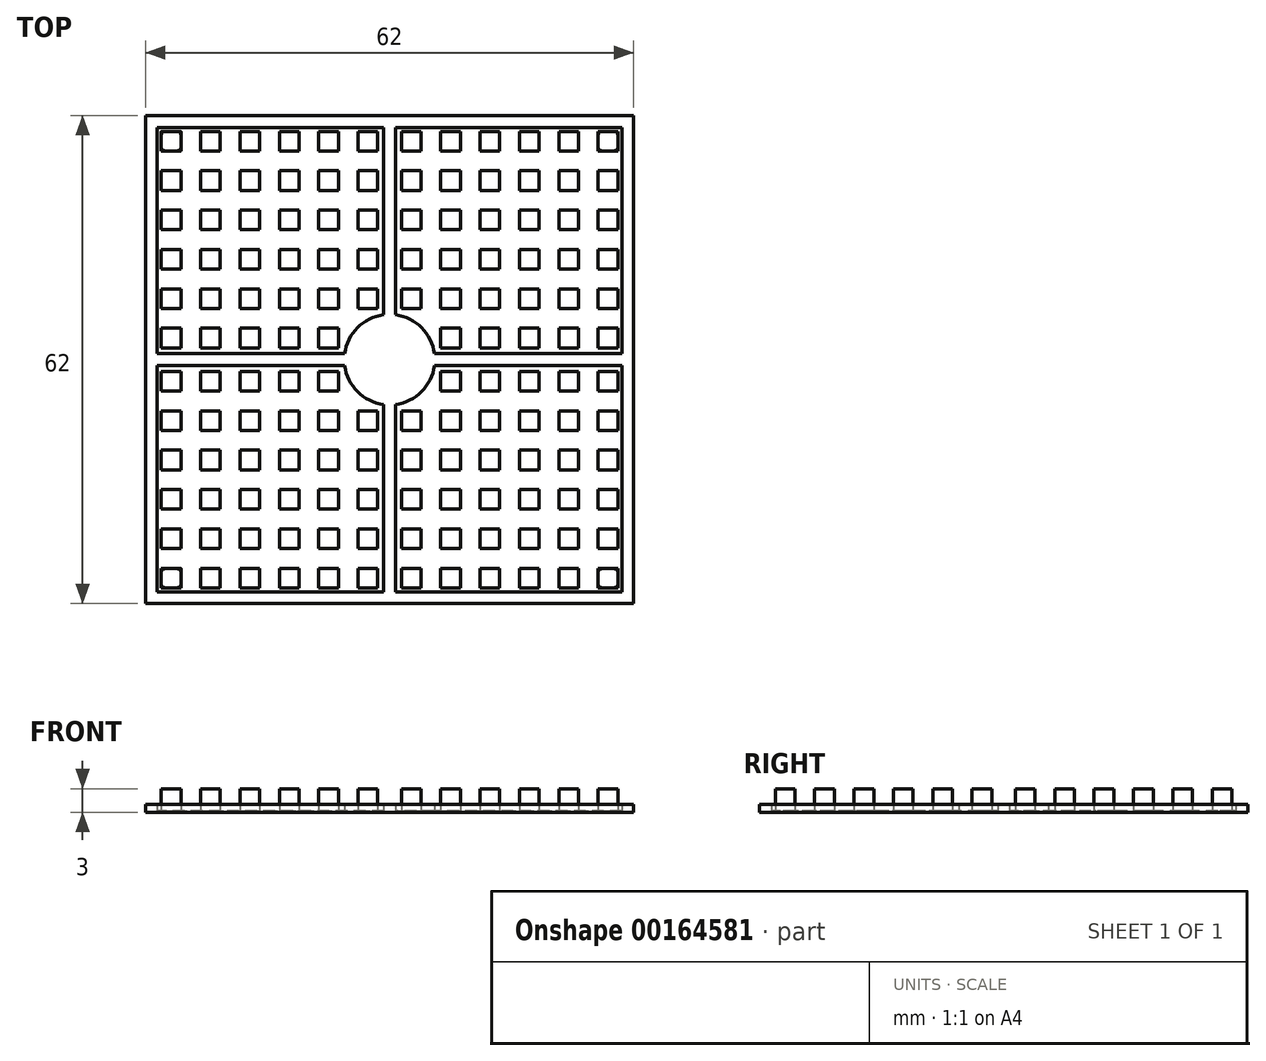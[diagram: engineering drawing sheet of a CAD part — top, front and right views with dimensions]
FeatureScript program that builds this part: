
annotation { "Feature Type Name" : "Feature", "Feature Type Description" : "" }
export const myFeature = defineFeature(function(context is Context, id is Id, definition is map)
    precondition{}
    {
        {
            var Q0;
            Q0=qCreatedBy(makeId("Top.planeOp"),FACE);
            var sketch = newSketch(context, id + "F0", { "sketchPlane" : qUnion([Q0])});
            skArc(sketch, "E0", {"start": v(-5.7, -0.75) * mm, "mid": v(-4.07, -4.07) * mm, "end": v(-0.75, -5.7) * mm});
            skLineSegment(sketch, "E1.bottom", {"start": v(31, 31) * mm, "end": v(-31, 31) * mm});
            skLineSegment(sketch, "E1.top", {"start": v(31, -31) * mm, "end": v(-31, -31) * mm});
            skLineSegment(sketch, "E1.left", {"start": v(31, 31) * mm, "end": v(31, -31) * mm});
            skLineSegment(sketch, "E1.right", {"start": v(-31, 31) * mm, "end": v(-31, -31) * mm});
            skLineSegment(sketch, "E2.bottom", {"start": v(-0.75, 29.5) * mm, "end": v(-29.5, 29.5) * mm});
            skLineSegment(sketch, "E2.top", {"start": v(-0.75, -29.5) * mm, "end": v(-29.5, -29.5) * mm});
            skLineSegment(sketch, "E2.right", {"start": v(-29.5, 29.5) * mm, "end": v(-29.5, -29.5) * mm});
            skLineSegment(sketch, "E3", {"start": v(0, 5.75) * mm, "end": v(0, 31) * mm, "construction": true});
            skLineSegment(sketch, "E4", {"start": v(0, 0) * mm, "end": v(31, 0) * mm, "construction": true});
            skLineSegment(sketch, "E5", {"start": v(0, -5.75) * mm, "end": v(0, -29.5) * mm, "construction": true});
            skLineSegment(sketch, "E6", {"start": v(0, 0) * mm, "end": v(-0.75, 0) * mm, "construction": true});
            skLineSegment(sketch, "E7", {"start": v(-0.75, 29.5) * mm, "end": v(-0.75, 5.7) * mm});
            skLineSegment(sketch, "E8", {"start": v(-29.5, -0.75) * mm, "end": v(-5.7, -0.75) * mm});
            skLineSegment(sketch, "E9", {"start": v(-29.5, 0.75) * mm, "end": v(-5.7, 0.75) * mm});
            skLineSegment(sketch, "E10.trimOffspring", {"start": v(-5.75, 0) * mm, "end": v(-31, 0) * mm, "construction": true});
            skArc(sketch, "E11.trimOffspring", {"start": v(-0.75, 5.7) * mm, "mid": v(-4.07, 4.07) * mm, "end": v(-5.7, 0.75) * mm});
            skPoint(sketch, "E12.orphan", {"position": v(29.5, -29.5) * mm});
            skPoint(sketch, "E13.orphan", {"position": v(29.5, 29.5) * mm});
            skLineSegment(sketch, "E14.MirrorCS", {"start": v(0.75, 29.5) * mm, "end": v(0.75, 5.7) * mm});
            skLineSegment(sketch, "E15.MirrorCS", {"start": v(0.75, 29.5) * mm, "end": v(29.5, 29.5) * mm});
            skLineSegment(sketch, "E16.MirrorCS", {"start": v(29.5, 29.5) * mm, "end": v(29.5, -29.5) * mm});
            skLineSegment(sketch, "E17.MirrorCS", {"start": v(29.5, 0.75) * mm, "end": v(5.7, 0.75) * mm});
            skLineSegment(sketch, "E18.MirrorCS", {"start": v(29.5, -0.75) * mm, "end": v(5.7, -0.75) * mm});
            skArc(sketch, "E19.MirrorCS", {"start": v(5.7, -0.75) * mm, "mid": v(4.07, -4.07) * mm, "end": v(0.75, -5.7) * mm});
            skArc(sketch, "E20.MirrorCS", {"start": v(0.75, 5.7) * mm, "mid": v(4.07, 4.07) * mm, "end": v(5.7, 0.75) * mm});
            skLineSegment(sketch, "E21.trimOffspring", {"start": v(-0.75, -5.7) * mm, "end": v(-0.75, -29.5) * mm});
            skLineSegment(sketch, "E22.trimOffspring", {"start": v(0.75, -5.7) * mm, "end": v(0.75, -29.5) * mm});
            skPoint(sketch, "E23.orphan", {"position": v(0, -5.75) * mm});
            skPoint(sketch, "E24.orphan", {"position": v(0, 5.75) * mm});
            skLineSegment(sketch, "E25.MirrorCS", {"start": v(0.75, -29.5) * mm, "end": v(29.5, -29.5) * mm});
            skPoint(sketch, "E26.orphan", {"position": v(0, -31) * mm});
            skPoint(sketch, "E27.orphan", {"position": v(0, -29.5) * mm});
            skPoint(sketch, "E28.orphan", {"position": v(0, 29.5) * mm});
            skSolve(sketch);
        }
        {
            var Q0;
            Q0 = qSketchRegion(id + "F0", true);
            extrude(context, id + "F1", {"entities" : qUnion([Q0]), "depth" : 1 * mm});
        }
        {
            var Q0;
            Q0=qCreatedBy(makeId("Top.planeOp"),FACE);
            var sketch = newSketch(context, id + "F2", { "sketchPlane" : qUnion([Q0])});
            skLineSegment(sketch, "E29.bottom", {"start": v(-29, 29) * mm, "end": v(-26.5, 29) * mm});
            skLineSegment(sketch, "E29.top", {"start": v(-29, 26.5) * mm, "end": v(-26.5, 26.5) * mm});
            skLineSegment(sketch, "E29.left", {"start": v(-29, 29) * mm, "end": v(-29, 26.5) * mm});
            skLineSegment(sketch, "E29.right", {"start": v(-26.5, 29) * mm, "end": v(-26.5, 26.5) * mm});
            skLineSegment(sketch, "E30.0.1.0", {"start": v(-29, 24) * mm, "end": v(-26.5, 24) * mm});
            skLineSegment(sketch, "E30.0.1.1", {"start": v(-29, 21.5) * mm, "end": v(-26.5, 21.5) * mm});
            skLineSegment(sketch, "E30.0.1.2", {"start": v(-29, 24) * mm, "end": v(-29, 21.5) * mm});
            skLineSegment(sketch, "E30.0.1.3", {"start": v(-26.5, 24) * mm, "end": v(-26.5, 21.5) * mm});
            skLineSegment(sketch, "E30.0.2.0", {"start": v(-29, 19) * mm, "end": v(-26.5, 19) * mm});
            skLineSegment(sketch, "E30.0.2.1", {"start": v(-29, 16.5) * mm, "end": v(-26.5, 16.5) * mm});
            skLineSegment(sketch, "E30.0.2.2", {"start": v(-29, 19) * mm, "end": v(-29, 16.5) * mm});
            skLineSegment(sketch, "E30.0.2.3", {"start": v(-26.5, 19) * mm, "end": v(-26.5, 16.5) * mm});
            skLineSegment(sketch, "E30.0.3.0", {"start": v(-29, 14) * mm, "end": v(-26.5, 14) * mm});
            skLineSegment(sketch, "E30.0.3.1", {"start": v(-29, 11.5) * mm, "end": v(-26.5, 11.5) * mm});
            skLineSegment(sketch, "E30.0.3.2", {"start": v(-29, 14) * mm, "end": v(-29, 11.5) * mm});
            skLineSegment(sketch, "E30.0.3.3", {"start": v(-26.5, 14) * mm, "end": v(-26.5, 11.5) * mm});
            skLineSegment(sketch, "E30.0.4.0", {"start": v(-29, 9) * mm, "end": v(-26.5, 9) * mm});
            skLineSegment(sketch, "E30.0.4.1", {"start": v(-29, 6.5) * mm, "end": v(-26.5, 6.5) * mm});
            skLineSegment(sketch, "E30.0.4.2", {"start": v(-29, 9) * mm, "end": v(-29, 6.5) * mm});
            skLineSegment(sketch, "E30.0.4.3", {"start": v(-26.5, 9) * mm, "end": v(-26.5, 6.5) * mm});
            skLineSegment(sketch, "E30.0.5.0", {"start": v(-29, 4) * mm, "end": v(-26.5, 4) * mm});
            skLineSegment(sketch, "E30.0.5.1", {"start": v(-29, 1.5) * mm, "end": v(-26.5, 1.5) * mm});
            skLineSegment(sketch, "E30.0.5.2", {"start": v(-29, 4) * mm, "end": v(-29, 1.5) * mm});
            skLineSegment(sketch, "E30.0.5.3", {"start": v(-26.5, 4) * mm, "end": v(-26.5, 1.5) * mm});
            skLineSegment(sketch, "E30.1.0.0", {"start": v(-24, 29) * mm, "end": v(-21.5, 29) * mm});
            skLineSegment(sketch, "E30.1.0.1", {"start": v(-24, 26.5) * mm, "end": v(-21.5, 26.5) * mm});
            skLineSegment(sketch, "E30.1.0.2", {"start": v(-24, 29) * mm, "end": v(-24, 26.5) * mm});
            skLineSegment(sketch, "E30.1.0.3", {"start": v(-21.5, 29) * mm, "end": v(-21.5, 26.5) * mm});
            skLineSegment(sketch, "E30.1.1.0", {"start": v(-24, 24) * mm, "end": v(-21.5, 24) * mm});
            skLineSegment(sketch, "E30.1.1.1", {"start": v(-24, 21.5) * mm, "end": v(-21.5, 21.5) * mm});
            skLineSegment(sketch, "E30.1.1.2", {"start": v(-24, 24) * mm, "end": v(-24, 21.5) * mm});
            skLineSegment(sketch, "E30.1.1.3", {"start": v(-21.5, 24) * mm, "end": v(-21.5, 21.5) * mm});
            skLineSegment(sketch, "E30.1.2.0", {"start": v(-24, 19) * mm, "end": v(-21.5, 19) * mm});
            skLineSegment(sketch, "E30.1.2.1", {"start": v(-24, 16.5) * mm, "end": v(-21.5, 16.5) * mm});
            skLineSegment(sketch, "E30.1.2.2", {"start": v(-24, 19) * mm, "end": v(-24, 16.5) * mm});
            skLineSegment(sketch, "E30.1.2.3", {"start": v(-21.5, 19) * mm, "end": v(-21.5, 16.5) * mm});
            skLineSegment(sketch, "E30.1.3.0", {"start": v(-24, 14) * mm, "end": v(-21.5, 14) * mm});
            skLineSegment(sketch, "E30.1.3.1", {"start": v(-24, 11.5) * mm, "end": v(-21.5, 11.5) * mm});
            skLineSegment(sketch, "E30.1.3.2", {"start": v(-24, 14) * mm, "end": v(-24, 11.5) * mm});
            skLineSegment(sketch, "E30.1.3.3", {"start": v(-21.5, 14) * mm, "end": v(-21.5, 11.5) * mm});
            skLineSegment(sketch, "E30.1.4.0", {"start": v(-24, 9) * mm, "end": v(-21.5, 9) * mm});
            skLineSegment(sketch, "E30.1.4.1", {"start": v(-24, 6.5) * mm, "end": v(-21.5, 6.5) * mm});
            skLineSegment(sketch, "E30.1.4.2", {"start": v(-24, 9) * mm, "end": v(-24, 6.5) * mm});
            skLineSegment(sketch, "E30.1.4.3", {"start": v(-21.5, 9) * mm, "end": v(-21.5, 6.5) * mm});
            skLineSegment(sketch, "E30.1.5.0", {"start": v(-24, 4) * mm, "end": v(-21.5, 4) * mm});
            skLineSegment(sketch, "E30.1.5.1", {"start": v(-24, 1.5) * mm, "end": v(-21.5, 1.5) * mm});
            skLineSegment(sketch, "E30.1.5.2", {"start": v(-24, 4) * mm, "end": v(-24, 1.5) * mm});
            skLineSegment(sketch, "E30.1.5.3", {"start": v(-21.5, 4) * mm, "end": v(-21.5, 1.5) * mm});
            skLineSegment(sketch, "E30.2.0.0", {"start": v(-19, 29) * mm, "end": v(-16.5, 29) * mm});
            skLineSegment(sketch, "E30.2.0.1", {"start": v(-19, 26.5) * mm, "end": v(-16.5, 26.5) * mm});
            skLineSegment(sketch, "E30.2.0.2", {"start": v(-19, 29) * mm, "end": v(-19, 26.5) * mm});
            skLineSegment(sketch, "E30.2.0.3", {"start": v(-16.5, 29) * mm, "end": v(-16.5, 26.5) * mm});
            skLineSegment(sketch, "E30.2.1.0", {"start": v(-19, 24) * mm, "end": v(-16.5, 24) * mm});
            skLineSegment(sketch, "E30.2.1.1", {"start": v(-19, 21.5) * mm, "end": v(-16.5, 21.5) * mm});
            skLineSegment(sketch, "E30.2.1.2", {"start": v(-19, 24) * mm, "end": v(-19, 21.5) * mm});
            skLineSegment(sketch, "E30.2.1.3", {"start": v(-16.5, 24) * mm, "end": v(-16.5, 21.5) * mm});
            skLineSegment(sketch, "E30.2.2.0", {"start": v(-19, 19) * mm, "end": v(-16.5, 19) * mm});
            skLineSegment(sketch, "E30.2.2.1", {"start": v(-19, 16.5) * mm, "end": v(-16.5, 16.5) * mm});
            skLineSegment(sketch, "E30.2.2.2", {"start": v(-19, 19) * mm, "end": v(-19, 16.5) * mm});
            skLineSegment(sketch, "E30.2.2.3", {"start": v(-16.5, 19) * mm, "end": v(-16.5, 16.5) * mm});
            skLineSegment(sketch, "E30.2.3.0", {"start": v(-19, 14) * mm, "end": v(-16.5, 14) * mm});
            skLineSegment(sketch, "E30.2.3.1", {"start": v(-19, 11.5) * mm, "end": v(-16.5, 11.5) * mm});
            skLineSegment(sketch, "E30.2.3.2", {"start": v(-19, 14) * mm, "end": v(-19, 11.5) * mm});
            skLineSegment(sketch, "E30.2.3.3", {"start": v(-16.5, 14) * mm, "end": v(-16.5, 11.5) * mm});
            skLineSegment(sketch, "E30.2.4.0", {"start": v(-19, 9) * mm, "end": v(-16.5, 9) * mm});
            skLineSegment(sketch, "E30.2.4.1", {"start": v(-19, 6.5) * mm, "end": v(-16.5, 6.5) * mm});
            skLineSegment(sketch, "E30.2.4.2", {"start": v(-19, 9) * mm, "end": v(-19, 6.5) * mm});
            skLineSegment(sketch, "E30.2.4.3", {"start": v(-16.5, 9) * mm, "end": v(-16.5, 6.5) * mm});
            skLineSegment(sketch, "E30.2.5.0", {"start": v(-19, 4) * mm, "end": v(-16.5, 4) * mm});
            skLineSegment(sketch, "E30.2.5.1", {"start": v(-19, 1.5) * mm, "end": v(-16.5, 1.5) * mm});
            skLineSegment(sketch, "E30.2.5.2", {"start": v(-19, 4) * mm, "end": v(-19, 1.5) * mm});
            skLineSegment(sketch, "E30.2.5.3", {"start": v(-16.5, 4) * mm, "end": v(-16.5, 1.5) * mm});
            skLineSegment(sketch, "E30.3.0.0", {"start": v(-14, 29) * mm, "end": v(-11.5, 29) * mm});
            skLineSegment(sketch, "E30.3.0.1", {"start": v(-14, 26.5) * mm, "end": v(-11.5, 26.5) * mm});
            skLineSegment(sketch, "E30.3.0.2", {"start": v(-14, 29) * mm, "end": v(-14, 26.5) * mm});
            skLineSegment(sketch, "E30.3.0.3", {"start": v(-11.5, 29) * mm, "end": v(-11.5, 26.5) * mm});
            skLineSegment(sketch, "E30.3.1.0", {"start": v(-14, 24) * mm, "end": v(-11.5, 24) * mm});
            skLineSegment(sketch, "E30.3.1.1", {"start": v(-14, 21.5) * mm, "end": v(-11.5, 21.5) * mm});
            skLineSegment(sketch, "E30.3.1.2", {"start": v(-14, 24) * mm, "end": v(-14, 21.5) * mm});
            skLineSegment(sketch, "E30.3.1.3", {"start": v(-11.5, 24) * mm, "end": v(-11.5, 21.5) * mm});
            skLineSegment(sketch, "E30.3.2.0", {"start": v(-14, 19) * mm, "end": v(-11.5, 19) * mm});
            skLineSegment(sketch, "E30.3.2.1", {"start": v(-14, 16.5) * mm, "end": v(-11.5, 16.5) * mm});
            skLineSegment(sketch, "E30.3.2.2", {"start": v(-14, 19) * mm, "end": v(-14, 16.5) * mm});
            skLineSegment(sketch, "E30.3.2.3", {"start": v(-11.5, 19) * mm, "end": v(-11.5, 16.5) * mm});
            skLineSegment(sketch, "E30.3.3.0", {"start": v(-14, 14) * mm, "end": v(-11.5, 14) * mm});
            skLineSegment(sketch, "E30.3.3.1", {"start": v(-14, 11.5) * mm, "end": v(-11.5, 11.5) * mm});
            skLineSegment(sketch, "E30.3.3.2", {"start": v(-14, 14) * mm, "end": v(-14, 11.5) * mm});
            skLineSegment(sketch, "E30.3.3.3", {"start": v(-11.5, 14) * mm, "end": v(-11.5, 11.5) * mm});
            skLineSegment(sketch, "E30.3.4.0", {"start": v(-14, 9) * mm, "end": v(-11.5, 9) * mm});
            skLineSegment(sketch, "E30.3.4.1", {"start": v(-14, 6.5) * mm, "end": v(-11.5, 6.5) * mm});
            skLineSegment(sketch, "E30.3.4.2", {"start": v(-14, 9) * mm, "end": v(-14, 6.5) * mm});
            skLineSegment(sketch, "E30.3.4.3", {"start": v(-11.5, 9) * mm, "end": v(-11.5, 6.5) * mm});
            skLineSegment(sketch, "E30.3.5.0", {"start": v(-14, 4) * mm, "end": v(-11.5, 4) * mm});
            skLineSegment(sketch, "E30.3.5.1", {"start": v(-14, 1.5) * mm, "end": v(-11.5, 1.5) * mm});
            skLineSegment(sketch, "E30.3.5.2", {"start": v(-14, 4) * mm, "end": v(-14, 1.5) * mm});
            skLineSegment(sketch, "E30.3.5.3", {"start": v(-11.5, 4) * mm, "end": v(-11.5, 1.5) * mm});
            skLineSegment(sketch, "E30.4.0.0", {"start": v(-9, 29) * mm, "end": v(-6.5, 29) * mm});
            skLineSegment(sketch, "E30.4.0.1", {"start": v(-9, 26.5) * mm, "end": v(-6.5, 26.5) * mm});
            skLineSegment(sketch, "E30.4.0.2", {"start": v(-9, 29) * mm, "end": v(-9, 26.5) * mm});
            skLineSegment(sketch, "E30.4.0.3", {"start": v(-6.5, 29) * mm, "end": v(-6.5, 26.5) * mm});
            skLineSegment(sketch, "E30.4.1.0", {"start": v(-9, 24) * mm, "end": v(-6.5, 24) * mm});
            skLineSegment(sketch, "E30.4.1.1", {"start": v(-9, 21.5) * mm, "end": v(-6.5, 21.5) * mm});
            skLineSegment(sketch, "E30.4.1.2", {"start": v(-9, 24) * mm, "end": v(-9, 21.5) * mm});
            skLineSegment(sketch, "E30.4.1.3", {"start": v(-6.5, 24) * mm, "end": v(-6.5, 21.5) * mm});
            skLineSegment(sketch, "E30.4.2.0", {"start": v(-9, 19) * mm, "end": v(-6.5, 19) * mm});
            skLineSegment(sketch, "E30.4.2.1", {"start": v(-9, 16.5) * mm, "end": v(-6.5, 16.5) * mm});
            skLineSegment(sketch, "E30.4.2.2", {"start": v(-9, 19) * mm, "end": v(-9, 16.5) * mm});
            skLineSegment(sketch, "E30.4.2.3", {"start": v(-6.5, 19) * mm, "end": v(-6.5, 16.5) * mm});
            skLineSegment(sketch, "E30.4.3.0", {"start": v(-9, 14) * mm, "end": v(-6.5, 14) * mm});
            skLineSegment(sketch, "E30.4.3.1", {"start": v(-9, 11.5) * mm, "end": v(-6.5, 11.5) * mm});
            skLineSegment(sketch, "E30.4.3.2", {"start": v(-9, 14) * mm, "end": v(-9, 11.5) * mm});
            skLineSegment(sketch, "E30.4.3.3", {"start": v(-6.5, 14) * mm, "end": v(-6.5, 11.5) * mm});
            skLineSegment(sketch, "E30.4.4.0", {"start": v(-9, 9) * mm, "end": v(-6.5, 9) * mm});
            skLineSegment(sketch, "E30.4.4.1", {"start": v(-9, 6.5) * mm, "end": v(-6.5, 6.5) * mm});
            skLineSegment(sketch, "E30.4.4.2", {"start": v(-9, 9) * mm, "end": v(-9, 6.5) * mm});
            skLineSegment(sketch, "E30.4.4.3", {"start": v(-6.5, 9) * mm, "end": v(-6.5, 6.5) * mm});
            skLineSegment(sketch, "E30.4.5.0", {"start": v(-9, 4) * mm, "end": v(-6.5, 4) * mm});
            skLineSegment(sketch, "E30.4.5.1", {"start": v(-9, 1.5) * mm, "end": v(-6.5, 1.5) * mm});
            skLineSegment(sketch, "E30.4.5.2", {"start": v(-9, 4) * mm, "end": v(-9, 1.5) * mm});
            skLineSegment(sketch, "E30.4.5.3", {"start": v(-6.5, 4) * mm, "end": v(-6.5, 1.5) * mm});
            skLineSegment(sketch, "E30.5.0.0", {"start": v(-4, 29) * mm, "end": v(-1.5, 29) * mm});
            skLineSegment(sketch, "E30.5.0.1", {"start": v(-4, 26.5) * mm, "end": v(-1.5, 26.5) * mm});
            skLineSegment(sketch, "E30.5.0.2", {"start": v(-4, 29) * mm, "end": v(-4, 26.5) * mm});
            skLineSegment(sketch, "E30.5.0.3", {"start": v(-1.5, 29) * mm, "end": v(-1.5, 26.5) * mm});
            skLineSegment(sketch, "E30.5.1.0", {"start": v(-4, 24) * mm, "end": v(-1.5, 24) * mm});
            skLineSegment(sketch, "E30.5.1.1", {"start": v(-4, 21.5) * mm, "end": v(-1.5, 21.5) * mm});
            skLineSegment(sketch, "E30.5.1.2", {"start": v(-4, 24) * mm, "end": v(-4, 21.5) * mm});
            skLineSegment(sketch, "E30.5.1.3", {"start": v(-1.5, 24) * mm, "end": v(-1.5, 21.5) * mm});
            skLineSegment(sketch, "E30.5.2.0", {"start": v(-4, 19) * mm, "end": v(-1.5, 19) * mm});
            skLineSegment(sketch, "E30.5.2.1", {"start": v(-4, 16.5) * mm, "end": v(-1.5, 16.5) * mm});
            skLineSegment(sketch, "E30.5.2.2", {"start": v(-4, 19) * mm, "end": v(-4, 16.5) * mm});
            skLineSegment(sketch, "E30.5.2.3", {"start": v(-1.5, 19) * mm, "end": v(-1.5, 16.5) * mm});
            skLineSegment(sketch, "E30.5.3.0", {"start": v(-4, 14) * mm, "end": v(-1.5, 14) * mm});
            skLineSegment(sketch, "E30.5.3.1", {"start": v(-4, 11.5) * mm, "end": v(-1.5, 11.5) * mm});
            skLineSegment(sketch, "E30.5.3.2", {"start": v(-4, 14) * mm, "end": v(-4, 11.5) * mm});
            skLineSegment(sketch, "E30.5.3.3", {"start": v(-1.5, 14) * mm, "end": v(-1.5, 11.5) * mm});
            skLineSegment(sketch, "E30.5.4.0", {"start": v(-4, 9) * mm, "end": v(-1.5, 9) * mm});
            skLineSegment(sketch, "E30.5.4.1", {"start": v(-4, 6.5) * mm, "end": v(-1.5, 6.5) * mm});
            skLineSegment(sketch, "E30.5.4.2", {"start": v(-4, 9) * mm, "end": v(-4, 6.5) * mm});
            skLineSegment(sketch, "E30.5.4.3", {"start": v(-1.5, 9) * mm, "end": v(-1.5, 6.5) * mm});
            skLineSegment(sketch, "E30.5.5.0", {"start": v(-4, 4) * mm, "end": v(-1.5, 4) * mm});
            skLineSegment(sketch, "E30.5.5.1", {"start": v(-4, 1.5) * mm, "end": v(-1.5, 1.5) * mm});
            skLineSegment(sketch, "E30.5.5.2", {"start": v(-4, 4) * mm, "end": v(-4, 1.5) * mm});
            skLineSegment(sketch, "E30.5.5.3", {"start": v(-1.5, 4) * mm, "end": v(-1.5, 1.5) * mm});
            skLineSegment(sketch, "E30.direction1", {"start": v(-29, 26.5) * mm, "end": v(-24, 26.5) * mm, "construction": true});
            skLineSegment(sketch, "E30.direction2", {"start": v(-29, 26.5) * mm, "end": v(-29, 21.5) * mm, "construction": true});
            skSolve(sketch);
        }
        {
            var Q0;
            Q0=makeQuery(id+"F2.imprint","IMPRINT",FACE,{"disambiguationData":[TD([[makeQuery(id+"F2.imprint","IMPRINT",EDGE,{"derivedFrom":sQuery(id+"F2.wireOp",EDGE,"E29.bottom")}),-1.0]])]});
            var Q1;
            Q1=makeQuery(id+"F2.imprint","IMPRINT",FACE,{"disambiguationData":[TD([[makeQuery(id+"F2.imprint","IMPRINT",EDGE,{"derivedFrom":sQuery(id+"F2.wireOp",EDGE,"E30.1.0.0")}),-1.0]])]});
            var Q2;
            Q2=makeQuery(id+"F2.imprint","IMPRINT",FACE,{"disambiguationData":[TD([[makeQuery(id+"F2.imprint","IMPRINT",EDGE,{"derivedFrom":sQuery(id+"F2.wireOp",EDGE,"E30.2.0.0")}),-1.0]])]});
            var Q3;
            Q3=makeQuery(id+"F2.imprint","IMPRINT",FACE,{"disambiguationData":[TD([[makeQuery(id+"F2.imprint","IMPRINT",EDGE,{"derivedFrom":sQuery(id+"F2.wireOp",EDGE,"E30.3.0.0")}),-1.0]])]});
            var Q4;
            Q4=makeQuery(id+"F2.imprint","IMPRINT",FACE,{"disambiguationData":[TD([[makeQuery(id+"F2.imprint","IMPRINT",EDGE,{"derivedFrom":sQuery(id+"F2.wireOp",EDGE,"E30.4.0.0")}),-1.0]])]});
            var Q5;
            Q5=makeQuery(id+"F2.imprint","IMPRINT",FACE,{"disambiguationData":[TD([[makeQuery(id+"F2.imprint","IMPRINT",EDGE,{"derivedFrom":sQuery(id+"F2.wireOp",EDGE,"E30.5.0.0")}),-1.0]])]});
            var Q6;
            Q6=makeQuery(id+"F2.imprint","IMPRINT",FACE,{"disambiguationData":[TD([[makeQuery(id+"F2.imprint","IMPRINT",EDGE,{"derivedFrom":sQuery(id+"F2.wireOp",EDGE,"E30.5.1.0")}),-1.0]])]});
            var Q7;
            Q7=makeQuery(id+"F2.imprint","IMPRINT",FACE,{"disambiguationData":[TD([[makeQuery(id+"F2.imprint","IMPRINT",EDGE,{"derivedFrom":sQuery(id+"F2.wireOp",EDGE,"E30.4.1.0")}),-1.0]])]});
            var Q8;
            Q8=makeQuery(id+"F2.imprint","IMPRINT",FACE,{"disambiguationData":[TD([[makeQuery(id+"F2.imprint","IMPRINT",EDGE,{"derivedFrom":sQuery(id+"F2.wireOp",EDGE,"E30.3.1.0")}),-1.0]])]});
            var Q9;
            Q9=makeQuery(id+"F2.imprint","IMPRINT",FACE,{"disambiguationData":[TD([[makeQuery(id+"F2.imprint","IMPRINT",EDGE,{"derivedFrom":sQuery(id+"F2.wireOp",EDGE,"E30.2.1.0")}),-1.0]])]});
            var Q10;
            Q10=makeQuery(id+"F2.imprint","IMPRINT",FACE,{"disambiguationData":[TD([[makeQuery(id+"F2.imprint","IMPRINT",EDGE,{"derivedFrom":sQuery(id+"F2.wireOp",EDGE,"E30.1.1.0")}),-1.0]])]});
            var Q11;
            Q11=makeQuery(id+"F2.imprint","IMPRINT",FACE,{"disambiguationData":[TD([[makeQuery(id+"F2.imprint","IMPRINT",EDGE,{"derivedFrom":sQuery(id+"F2.wireOp",EDGE,"E30.0.1.0")}),-1.0]])]});
            var Q12;
            Q12=makeQuery(id+"F2.imprint","IMPRINT",FACE,{"disambiguationData":[TD([[makeQuery(id+"F2.imprint","IMPRINT",EDGE,{"derivedFrom":sQuery(id+"F2.wireOp",EDGE,"E30.0.2.0")}),-1.0]])]});
            var Q13;
            Q13=makeQuery(id+"F2.imprint","IMPRINT",FACE,{"disambiguationData":[TD([[makeQuery(id+"F2.imprint","IMPRINT",EDGE,{"derivedFrom":sQuery(id+"F2.wireOp",EDGE,"E30.1.2.0")}),-1.0]])]});
            var Q14;
            Q14=makeQuery(id+"F2.imprint","IMPRINT",FACE,{"disambiguationData":[TD([[makeQuery(id+"F2.imprint","IMPRINT",EDGE,{"derivedFrom":sQuery(id+"F2.wireOp",EDGE,"E30.2.2.0")}),-1.0]])]});
            var Q15;
            Q15=makeQuery(id+"F2.imprint","IMPRINT",FACE,{"disambiguationData":[TD([[makeQuery(id+"F2.imprint","IMPRINT",EDGE,{"derivedFrom":sQuery(id+"F2.wireOp",EDGE,"E30.3.2.0")}),-1.0]])]});
            var Q16;
            Q16=makeQuery(id+"F2.imprint","IMPRINT",FACE,{"disambiguationData":[TD([[makeQuery(id+"F2.imprint","IMPRINT",EDGE,{"derivedFrom":sQuery(id+"F2.wireOp",EDGE,"E30.4.2.0")}),-1.0]])]});
            var Q17;
            Q17=makeQuery(id+"F2.imprint","IMPRINT",FACE,{"disambiguationData":[TD([[makeQuery(id+"F2.imprint","IMPRINT",EDGE,{"derivedFrom":sQuery(id+"F2.wireOp",EDGE,"E30.5.2.0")}),-1.0]])]});
            var Q18;
            Q18=makeQuery(id+"F2.imprint","IMPRINT",FACE,{"disambiguationData":[TD([[makeQuery(id+"F2.imprint","IMPRINT",EDGE,{"derivedFrom":sQuery(id+"F2.wireOp",EDGE,"E30.5.3.0")}),-1.0]])]});
            var Q19;
            Q19=makeQuery(id+"F2.imprint","IMPRINT",FACE,{"disambiguationData":[TD([[makeQuery(id+"F2.imprint","IMPRINT",EDGE,{"derivedFrom":sQuery(id+"F2.wireOp",EDGE,"E30.5.4.0")}),-1.0]])]});
            var Q20;
            Q20=makeQuery(id+"F2.imprint","IMPRINT",FACE,{"disambiguationData":[TD([[makeQuery(id+"F2.imprint","IMPRINT",EDGE,{"derivedFrom":sQuery(id+"F2.wireOp",EDGE,"E30.4.4.0")}),-1.0]])]});
            var Q21;
            Q21=makeQuery(id+"F2.imprint","IMPRINT",FACE,{"disambiguationData":[TD([[makeQuery(id+"F2.imprint","IMPRINT",EDGE,{"derivedFrom":sQuery(id+"F2.wireOp",EDGE,"E30.4.3.0")}),-1.0]])]});
            var Q22;
            Q22=makeQuery(id+"F2.imprint","IMPRINT",FACE,{"disambiguationData":[TD([[makeQuery(id+"F2.imprint","IMPRINT",EDGE,{"derivedFrom":sQuery(id+"F2.wireOp",EDGE,"E30.3.3.0")}),-1.0]])]});
            var Q23;
            Q23=makeQuery(id+"F2.imprint","IMPRINT",FACE,{"disambiguationData":[TD([[makeQuery(id+"F2.imprint","IMPRINT",EDGE,{"derivedFrom":sQuery(id+"F2.wireOp",EDGE,"E30.3.4.0")}),-1.0]])]});
            var Q24;
            Q24=makeQuery(id+"F2.imprint","IMPRINT",FACE,{"disambiguationData":[TD([[makeQuery(id+"F2.imprint","IMPRINT",EDGE,{"derivedFrom":sQuery(id+"F2.wireOp",EDGE,"E30.2.4.0")}),-1.0]])]});
            var Q25;
            Q25=makeQuery(id+"F2.imprint","IMPRINT",FACE,{"disambiguationData":[TD([[makeQuery(id+"F2.imprint","IMPRINT",EDGE,{"derivedFrom":sQuery(id+"F2.wireOp",EDGE,"E30.2.3.0")}),-1.0]])]});
            var Q26;
            Q26=makeQuery(id+"F2.imprint","IMPRINT",FACE,{"disambiguationData":[TD([[makeQuery(id+"F2.imprint","IMPRINT",EDGE,{"derivedFrom":sQuery(id+"F2.wireOp",EDGE,"E30.1.3.0")}),-1.0]])]});
            var Q27;
            Q27=makeQuery(id+"F2.imprint","IMPRINT",FACE,{"disambiguationData":[TD([[makeQuery(id+"F2.imprint","IMPRINT",EDGE,{"derivedFrom":sQuery(id+"F2.wireOp",EDGE,"E30.1.4.0")}),-1.0]])]});
            var Q28;
            Q28=makeQuery(id+"F2.imprint","IMPRINT",FACE,{"disambiguationData":[TD([[makeQuery(id+"F2.imprint","IMPRINT",EDGE,{"derivedFrom":sQuery(id+"F2.wireOp",EDGE,"E30.0.4.0")}),-1.0]])]});
            var Q29;
            Q29=makeQuery(id+"F2.imprint","IMPRINT",FACE,{"disambiguationData":[TD([[makeQuery(id+"F2.imprint","IMPRINT",EDGE,{"derivedFrom":sQuery(id+"F2.wireOp",EDGE,"E30.0.3.0")}),-1.0]])]});
            var Q30;
            Q30=makeQuery(id+"F2.imprint","IMPRINT",FACE,{"disambiguationData":[TD([[makeQuery(id+"F2.imprint","IMPRINT",EDGE,{"derivedFrom":sQuery(id+"F2.wireOp",EDGE,"E30.0.5.0")}),-1.0]])]});
            var Q31;
            Q31=makeQuery(id+"F2.imprint","IMPRINT",FACE,{"disambiguationData":[TD([[makeQuery(id+"F2.imprint","IMPRINT",EDGE,{"derivedFrom":sQuery(id+"F2.wireOp",EDGE,"E30.1.5.0")}),-1.0]])]});
            var Q32;
            Q32=makeQuery(id+"F2.imprint","IMPRINT",FACE,{"disambiguationData":[TD([[makeQuery(id+"F2.imprint","IMPRINT",EDGE,{"derivedFrom":sQuery(id+"F2.wireOp",EDGE,"E30.2.5.0")}),-1.0]])]});
            var Q33;
            Q33=makeQuery(id+"F2.imprint","IMPRINT",FACE,{"disambiguationData":[TD([[makeQuery(id+"F2.imprint","IMPRINT",EDGE,{"derivedFrom":sQuery(id+"F2.wireOp",EDGE,"E30.3.5.0")}),-1.0]])]});
            var Q34;
            Q34=makeQuery(id+"F2.imprint","IMPRINT",FACE,{"disambiguationData":[TD([[makeQuery(id+"F2.imprint","IMPRINT",EDGE,{"derivedFrom":sQuery(id+"F2.wireOp",EDGE,"E30.4.5.0")}),-1.0]])]});
            extrude(context, id + "F3", {"entities" : qUnion([Q0, Q1, Q2, Q3, Q4, Q5, Q6, Q7, Q8, Q9, Q10, Q11, Q12, Q13, Q14, Q15, Q16, Q17, Q18, Q19, Q20, Q21, Q22, Q23, Q24, Q25, Q26, Q27, Q28, Q29, Q30, Q31, Q32, Q33, Q34]), "operationType" : NewBodyOperationType.ADD, "depth" : 3 * mm});
        }
        {
            var Q0;
            Q0=makeQuery(id+"F3.opExtrude","CAP_EDGE",EDGE,{"disambiguationData":[OSD([sQuery(id+"F2.wireOp",EDGE,"E29.top")])],"isStart":false});
            var Q1;
            Q1=makeQuery(id+"F3.opExtrude","CAP_EDGE",EDGE,{"disambiguationData":[OSD([sQuery(id+"F2.wireOp",EDGE,"E29.left")])],"isStart":false});
            var Q2;
            Q2=makeQuery(id+"F3.opExtrude","CAP_EDGE",EDGE,{"disambiguationData":[OSD([sQuery(id+"F2.wireOp",EDGE,"E29.bottom")])],"isStart":false});
            var Q3;
            Q3=makeQuery(id+"F3.opExtrude","CAP_EDGE",EDGE,{"disambiguationData":[OSD([sQuery(id+"F2.wireOp",EDGE,"E29.right")])],"isStart":false});
            fillet(context, id + "F4", {"entities" : qUnion([Q0, Q1, Q2, Q3]), "radius" : 0.25 * mm, "tangentPropagation" : true, "rho" : 0.1, "crossSection" : FilletCrossSection.CONIC, "allowEdgeOverflow" : false});
        }
        {
            var Q0;
            Q0=makeQuery(id+"F3.opExtrude","SWEPT_BODY",BODY,{"disambiguationData":[OSD([sQuery(id+"F2.wireOp",EDGE,"E29.bottom"),sQuery(id+"F2.wireOp",EDGE,"E29.top"),sQuery(id+"F2.wireOp",EDGE,"E29.left"),sQuery(id+"F2.wireOp",EDGE,"E29.right")])]});
            var Q1;
            Q1=makeQuery(id+"F3.opExtrude","SWEPT_BODY",BODY,{"disambiguationData":[OSD([sQuery(id+"F2.wireOp",EDGE,"E30.1.0.0"),sQuery(id+"F2.wireOp",EDGE,"E30.1.0.1"),sQuery(id+"F2.wireOp",EDGE,"E30.1.0.2"),sQuery(id+"F2.wireOp",EDGE,"E30.1.0.3")])]});
            var Q2;
            Q2=makeQuery(id+"F3.opExtrude","SWEPT_BODY",BODY,{"disambiguationData":[OSD([sQuery(id+"F2.wireOp",EDGE,"E30.2.0.0"),sQuery(id+"F2.wireOp",EDGE,"E30.2.0.1"),sQuery(id+"F2.wireOp",EDGE,"E30.2.0.2"),sQuery(id+"F2.wireOp",EDGE,"E30.2.0.3")])]});
            var Q3;
            Q3=makeQuery(id+"F3.opExtrude","SWEPT_BODY",BODY,{"disambiguationData":[OSD([sQuery(id+"F2.wireOp",EDGE,"E30.3.0.0"),sQuery(id+"F2.wireOp",EDGE,"E30.3.0.1"),sQuery(id+"F2.wireOp",EDGE,"E30.3.0.2"),sQuery(id+"F2.wireOp",EDGE,"E30.3.0.3")])]});
            var Q4;
            Q4=makeQuery(id+"F3.opExtrude","SWEPT_BODY",BODY,{"disambiguationData":[OSD([sQuery(id+"F2.wireOp",EDGE,"E30.4.0.0"),sQuery(id+"F2.wireOp",EDGE,"E30.4.0.1"),sQuery(id+"F2.wireOp",EDGE,"E30.4.0.2"),sQuery(id+"F2.wireOp",EDGE,"E30.4.0.3")])]});
            var Q5;
            Q5=makeQuery(id+"F3.opExtrude","SWEPT_BODY",BODY,{"disambiguationData":[OSD([sQuery(id+"F2.wireOp",EDGE,"E30.5.0.0"),sQuery(id+"F2.wireOp",EDGE,"E30.5.0.1"),sQuery(id+"F2.wireOp",EDGE,"E30.5.0.2"),sQuery(id+"F2.wireOp",EDGE,"E30.5.0.3")])]});
            var Q6;
            Q6=makeQuery(id+"F3.opExtrude","SWEPT_BODY",BODY,{"disambiguationData":[OSD([sQuery(id+"F2.wireOp",EDGE,"E30.5.1.0"),sQuery(id+"F2.wireOp",EDGE,"E30.5.1.1"),sQuery(id+"F2.wireOp",EDGE,"E30.5.1.2"),sQuery(id+"F2.wireOp",EDGE,"E30.5.1.3")])]});
            var Q7;
            Q7=makeQuery(id+"F3.opExtrude","SWEPT_BODY",BODY,{"disambiguationData":[OSD([sQuery(id+"F2.wireOp",EDGE,"E30.5.2.0"),sQuery(id+"F2.wireOp",EDGE,"E30.5.2.1"),sQuery(id+"F2.wireOp",EDGE,"E30.5.2.2"),sQuery(id+"F2.wireOp",EDGE,"E30.5.2.3")])]});
            var Q8;
            Q8=makeQuery(id+"F3.opExtrude","SWEPT_BODY",BODY,{"disambiguationData":[OSD([sQuery(id+"F2.wireOp",EDGE,"E30.4.2.0"),sQuery(id+"F2.wireOp",EDGE,"E30.4.2.1"),sQuery(id+"F2.wireOp",EDGE,"E30.4.2.2"),sQuery(id+"F2.wireOp",EDGE,"E30.4.2.3")])]});
            var Q9;
            Q9=makeQuery(id+"F3.opExtrude","SWEPT_BODY",BODY,{"disambiguationData":[OSD([sQuery(id+"F2.wireOp",EDGE,"E30.4.1.0"),sQuery(id+"F2.wireOp",EDGE,"E30.4.1.1"),sQuery(id+"F2.wireOp",EDGE,"E30.4.1.2"),sQuery(id+"F2.wireOp",EDGE,"E30.4.1.3")])]});
            var Q10;
            Q10=makeQuery(id+"F3.opExtrude","SWEPT_BODY",BODY,{"disambiguationData":[OSD([sQuery(id+"F2.wireOp",EDGE,"E30.3.1.0"),sQuery(id+"F2.wireOp",EDGE,"E30.3.1.1"),sQuery(id+"F2.wireOp",EDGE,"E30.3.1.2"),sQuery(id+"F2.wireOp",EDGE,"E30.3.1.3")])]});
            var Q11;
            Q11=makeQuery(id+"F3.opExtrude","SWEPT_BODY",BODY,{"disambiguationData":[OSD([sQuery(id+"F2.wireOp",EDGE,"E30.4.5.0"),sQuery(id+"F2.wireOp",EDGE,"E30.4.5.1"),sQuery(id+"F2.wireOp",EDGE,"E30.4.5.2"),sQuery(id+"F2.wireOp",EDGE,"E30.4.5.3")])]});
            var Q12;
            Q12=makeQuery(id+"F3.opExtrude","SWEPT_BODY",BODY,{"disambiguationData":[OSD([sQuery(id+"F2.wireOp",EDGE,"E30.4.4.0"),sQuery(id+"F2.wireOp",EDGE,"E30.4.4.1"),sQuery(id+"F2.wireOp",EDGE,"E30.4.4.2"),sQuery(id+"F2.wireOp",EDGE,"E30.4.4.3")])]});
            var Q13;
            Q13=makeQuery(id+"F3.opExtrude","SWEPT_BODY",BODY,{"disambiguationData":[OSD([sQuery(id+"F2.wireOp",EDGE,"E30.1.1.0"),sQuery(id+"F2.wireOp",EDGE,"E30.1.1.1"),sQuery(id+"F2.wireOp",EDGE,"E30.1.1.2"),sQuery(id+"F2.wireOp",EDGE,"E30.1.1.3")])]});
            var Q14;
            Q14=makeQuery(id+"F3.opExtrude","SWEPT_BODY",BODY,{"disambiguationData":[OSD([sQuery(id+"F2.wireOp",EDGE,"E30.1.4.0"),sQuery(id+"F2.wireOp",EDGE,"E30.1.4.1"),sQuery(id+"F2.wireOp",EDGE,"E30.1.4.2"),sQuery(id+"F2.wireOp",EDGE,"E30.1.4.3")])]});
            var Q15;
            Q15=makeQuery(id+"F3.opExtrude","SWEPT_BODY",BODY,{"disambiguationData":[OSD([sQuery(id+"F2.wireOp",EDGE,"E30.1.5.0"),sQuery(id+"F2.wireOp",EDGE,"E30.1.5.1"),sQuery(id+"F2.wireOp",EDGE,"E30.1.5.2"),sQuery(id+"F2.wireOp",EDGE,"E30.1.5.3")])]});
            var Q16;
            Q16=makeQuery(id+"F3.opExtrude","SWEPT_BODY",BODY,{"disambiguationData":[OSD([sQuery(id+"F2.wireOp",EDGE,"E30.1.3.0"),sQuery(id+"F2.wireOp",EDGE,"E30.1.3.1"),sQuery(id+"F2.wireOp",EDGE,"E30.1.3.2"),sQuery(id+"F2.wireOp",EDGE,"E30.1.3.3")])]});
            var Q17;
            Q17=makeQuery(id+"F3.opExtrude","SWEPT_BODY",BODY,{"disambiguationData":[OSD([sQuery(id+"F2.wireOp",EDGE,"E30.1.2.0"),sQuery(id+"F2.wireOp",EDGE,"E30.1.2.1"),sQuery(id+"F2.wireOp",EDGE,"E30.1.2.2"),sQuery(id+"F2.wireOp",EDGE,"E30.1.2.3")])]});
            var Q18;
            Q18=makeQuery(id+"F3.opExtrude","SWEPT_BODY",BODY,{"disambiguationData":[OSD([sQuery(id+"F2.wireOp",EDGE,"E30.2.3.0"),sQuery(id+"F2.wireOp",EDGE,"E30.2.3.1"),sQuery(id+"F2.wireOp",EDGE,"E30.2.3.2"),sQuery(id+"F2.wireOp",EDGE,"E30.2.3.3")])]});
            var Q19;
            Q19=makeQuery(id+"F3.opExtrude","SWEPT_BODY",BODY,{"disambiguationData":[OSD([sQuery(id+"F2.wireOp",EDGE,"E30.2.4.0"),sQuery(id+"F2.wireOp",EDGE,"E30.2.4.1"),sQuery(id+"F2.wireOp",EDGE,"E30.2.4.2"),sQuery(id+"F2.wireOp",EDGE,"E30.2.4.3")])]});
            var Q20;
            Q20=makeQuery(id+"F3.opExtrude","SWEPT_BODY",BODY,{"disambiguationData":[OSD([sQuery(id+"F2.wireOp",EDGE,"E30.2.1.0"),sQuery(id+"F2.wireOp",EDGE,"E30.2.1.1"),sQuery(id+"F2.wireOp",EDGE,"E30.2.1.2"),sQuery(id+"F2.wireOp",EDGE,"E30.2.1.3")])]});
            var Q21;
            Q21=makeQuery(id+"F3.opExtrude","SWEPT_BODY",BODY,{"disambiguationData":[OSD([sQuery(id+"F2.wireOp",EDGE,"E30.2.2.0"),sQuery(id+"F2.wireOp",EDGE,"E30.2.2.1"),sQuery(id+"F2.wireOp",EDGE,"E30.2.2.2"),sQuery(id+"F2.wireOp",EDGE,"E30.2.2.3")])]});
            var Q22;
            Q22=makeQuery(id+"F3.opExtrude","SWEPT_BODY",BODY,{"disambiguationData":[OSD([sQuery(id+"F2.wireOp",EDGE,"E30.2.5.0"),sQuery(id+"F2.wireOp",EDGE,"E30.2.5.1"),sQuery(id+"F2.wireOp",EDGE,"E30.2.5.2"),sQuery(id+"F2.wireOp",EDGE,"E30.2.5.3")])]});
            var Q23;
            Q23=makeQuery(id+"F3.opExtrude","SWEPT_BODY",BODY,{"disambiguationData":[OSD([sQuery(id+"F2.wireOp",EDGE,"E30.0.5.0"),sQuery(id+"F2.wireOp",EDGE,"E30.0.5.1"),sQuery(id+"F2.wireOp",EDGE,"E30.0.5.2"),sQuery(id+"F2.wireOp",EDGE,"E30.0.5.3")])]});
            var Q24;
            Q24=makeQuery(id+"F3.opExtrude","SWEPT_BODY",BODY,{"disambiguationData":[OSD([sQuery(id+"F2.wireOp",EDGE,"E30.3.3.0"),sQuery(id+"F2.wireOp",EDGE,"E30.3.3.1"),sQuery(id+"F2.wireOp",EDGE,"E30.3.3.2"),sQuery(id+"F2.wireOp",EDGE,"E30.3.3.3")])]});
            var Q25;
            Q25=makeQuery(id+"F3.opExtrude","SWEPT_BODY",BODY,{"disambiguationData":[OSD([sQuery(id+"F2.wireOp",EDGE,"E30.3.2.0"),sQuery(id+"F2.wireOp",EDGE,"E30.3.2.1"),sQuery(id+"F2.wireOp",EDGE,"E30.3.2.2"),sQuery(id+"F2.wireOp",EDGE,"E30.3.2.3")])]});
            var Q26;
            Q26=makeQuery(id+"F3.opExtrude","SWEPT_BODY",BODY,{"disambiguationData":[OSD([sQuery(id+"F2.wireOp",EDGE,"E30.3.4.0"),sQuery(id+"F2.wireOp",EDGE,"E30.3.4.1"),sQuery(id+"F2.wireOp",EDGE,"E30.3.4.2"),sQuery(id+"F2.wireOp",EDGE,"E30.3.4.3")])]});
            var Q27;
            Q27=makeQuery(id+"F3.opExtrude","SWEPT_BODY",BODY,{"disambiguationData":[OSD([sQuery(id+"F2.wireOp",EDGE,"E30.0.3.0"),sQuery(id+"F2.wireOp",EDGE,"E30.0.3.1"),sQuery(id+"F2.wireOp",EDGE,"E30.0.3.2"),sQuery(id+"F2.wireOp",EDGE,"E30.0.3.3")])]});
            var Q28;
            Q28=makeQuery(id+"F3.opExtrude","SWEPT_BODY",BODY,{"disambiguationData":[OSD([sQuery(id+"F2.wireOp",EDGE,"E30.0.2.0"),sQuery(id+"F2.wireOp",EDGE,"E30.0.2.1"),sQuery(id+"F2.wireOp",EDGE,"E30.0.2.2"),sQuery(id+"F2.wireOp",EDGE,"E30.0.2.3")])]});
            var Q29;
            Q29=makeQuery(id+"F3.opExtrude","SWEPT_BODY",BODY,{"disambiguationData":[OSD([sQuery(id+"F2.wireOp",EDGE,"E30.3.5.0"),sQuery(id+"F2.wireOp",EDGE,"E30.3.5.1"),sQuery(id+"F2.wireOp",EDGE,"E30.3.5.2"),sQuery(id+"F2.wireOp",EDGE,"E30.3.5.3")])]});
            var Q30;
            Q30=makeQuery(id+"F3.opExtrude","SWEPT_BODY",BODY,{"disambiguationData":[OSD([sQuery(id+"F2.wireOp",EDGE,"E30.4.3.0"),sQuery(id+"F2.wireOp",EDGE,"E30.4.3.1"),sQuery(id+"F2.wireOp",EDGE,"E30.4.3.2"),sQuery(id+"F2.wireOp",EDGE,"E30.4.3.3")])]});
            var Q31;
            Q31=makeQuery(id+"F3.opExtrude","SWEPT_BODY",BODY,{"disambiguationData":[OSD([sQuery(id+"F2.wireOp",EDGE,"E30.5.3.0"),sQuery(id+"F2.wireOp",EDGE,"E30.5.3.1"),sQuery(id+"F2.wireOp",EDGE,"E30.5.3.2"),sQuery(id+"F2.wireOp",EDGE,"E30.5.3.3")])]});
            var Q32;
            Q32=makeQuery(id+"F3.opExtrude","SWEPT_BODY",BODY,{"disambiguationData":[OSD([sQuery(id+"F2.wireOp",EDGE,"E30.5.4.0"),sQuery(id+"F2.wireOp",EDGE,"E30.5.4.1"),sQuery(id+"F2.wireOp",EDGE,"E30.5.4.2"),sQuery(id+"F2.wireOp",EDGE,"E30.5.4.3")])]});
            var Q33;
            Q33=makeQuery(id+"F3.opExtrude","SWEPT_BODY",BODY,{"disambiguationData":[OSD([sQuery(id+"F2.wireOp",EDGE,"E30.0.1.0"),sQuery(id+"F2.wireOp",EDGE,"E30.0.1.1"),sQuery(id+"F2.wireOp",EDGE,"E30.0.1.2"),sQuery(id+"F2.wireOp",EDGE,"E30.0.1.3")])]});
            var Q34;
            Q34=makeQuery(id+"F3.opExtrude","SWEPT_BODY",BODY,{"disambiguationData":[OSD([sQuery(id+"F2.wireOp",EDGE,"E30.0.4.0"),sQuery(id+"F2.wireOp",EDGE,"E30.0.4.1"),sQuery(id+"F2.wireOp",EDGE,"E30.0.4.2"),sQuery(id+"F2.wireOp",EDGE,"E30.0.4.3")])]});
            var Q35;
            Q35=qCreatedBy(makeId("Right.planeOp"),FACE);
            mirror(context, id + "F5", {"entities" : qUnion([Q0, Q1, Q2, Q3, Q4, Q5, Q6, Q7, Q8, Q9, Q10, Q11, Q12, Q13, Q14, Q15, Q16, Q17, Q18, Q19, Q20, Q21, Q22, Q23, Q24, Q25, Q26, Q27, Q28, Q29, Q30, Q31, Q32, Q33, Q34]), "mirrorPlane" : qUnion([Q35])});
        }
        {
            var Q0;
            Q0=makeQuery(id+"F3.opExtrude","SWEPT_BODY",BODY,{"disambiguationData":[OSD([sQuery(id+"F2.wireOp",EDGE,"E30.1.0.0"),sQuery(id+"F2.wireOp",EDGE,"E30.1.0.1"),sQuery(id+"F2.wireOp",EDGE,"E30.1.0.2"),sQuery(id+"F2.wireOp",EDGE,"E30.1.0.3")])]});
            var Q1;
            Q1=makeQuery(id+"F3.opExtrude","SWEPT_BODY",BODY,{"disambiguationData":[OSD([sQuery(id+"F2.wireOp",EDGE,"E30.5.0.0"),sQuery(id+"F2.wireOp",EDGE,"E30.5.0.1"),sQuery(id+"F2.wireOp",EDGE,"E30.5.0.2"),sQuery(id+"F2.wireOp",EDGE,"E30.5.0.3")])]});
            var Q2;
            Q2=makeQuery(id+"F3.opExtrude","SWEPT_BODY",BODY,{"disambiguationData":[OSD([sQuery(id+"F2.wireOp",EDGE,"E30.4.5.0"),sQuery(id+"F2.wireOp",EDGE,"E30.4.5.1"),sQuery(id+"F2.wireOp",EDGE,"E30.4.5.2"),sQuery(id+"F2.wireOp",EDGE,"E30.4.5.3")])]});
            var Q3;
            Q3=makeQuery(id+"F3.opExtrude","SWEPT_BODY",BODY,{"disambiguationData":[OSD([sQuery(id+"F2.wireOp",EDGE,"E30.4.4.0"),sQuery(id+"F2.wireOp",EDGE,"E30.4.4.1"),sQuery(id+"F2.wireOp",EDGE,"E30.4.4.2"),sQuery(id+"F2.wireOp",EDGE,"E30.4.4.3")])]});
            var Q4;
            Q4=makeQuery(id+"F3.opExtrude","SWEPT_BODY",BODY,{"disambiguationData":[OSD([sQuery(id+"F2.wireOp",EDGE,"E30.5.1.0"),sQuery(id+"F2.wireOp",EDGE,"E30.5.1.1"),sQuery(id+"F2.wireOp",EDGE,"E30.5.1.2"),sQuery(id+"F2.wireOp",EDGE,"E30.5.1.3")])]});
            var Q5;
            Q5=makeQuery(id+"F3.opExtrude","SWEPT_BODY",BODY,{"disambiguationData":[OSD([sQuery(id+"F2.wireOp",EDGE,"E30.1.1.0"),sQuery(id+"F2.wireOp",EDGE,"E30.1.1.1"),sQuery(id+"F2.wireOp",EDGE,"E30.1.1.2"),sQuery(id+"F2.wireOp",EDGE,"E30.1.1.3")])]});
            var Q6;
            Q6=makeQuery(id+"F3.opExtrude","SWEPT_BODY",BODY,{"disambiguationData":[OSD([sQuery(id+"F2.wireOp",EDGE,"E30.1.4.0"),sQuery(id+"F2.wireOp",EDGE,"E30.1.4.1"),sQuery(id+"F2.wireOp",EDGE,"E30.1.4.2"),sQuery(id+"F2.wireOp",EDGE,"E30.1.4.3")])]});
            var Q7;
            Q7=makeQuery(id+"F3.opExtrude","SWEPT_BODY",BODY,{"disambiguationData":[OSD([sQuery(id+"F2.wireOp",EDGE,"E30.1.5.0"),sQuery(id+"F2.wireOp",EDGE,"E30.1.5.1"),sQuery(id+"F2.wireOp",EDGE,"E30.1.5.2"),sQuery(id+"F2.wireOp",EDGE,"E30.1.5.3")])]});
            var Q8;
            Q8=makeQuery(id+"F3.opExtrude","SWEPT_BODY",BODY,{"disambiguationData":[OSD([sQuery(id+"F2.wireOp",EDGE,"E30.1.3.0"),sQuery(id+"F2.wireOp",EDGE,"E30.1.3.1"),sQuery(id+"F2.wireOp",EDGE,"E30.1.3.2"),sQuery(id+"F2.wireOp",EDGE,"E30.1.3.3")])]});
            var Q9;
            Q9=makeQuery(id+"F3.opExtrude","SWEPT_BODY",BODY,{"disambiguationData":[OSD([sQuery(id+"F2.wireOp",EDGE,"E30.1.2.0"),sQuery(id+"F2.wireOp",EDGE,"E30.1.2.1"),sQuery(id+"F2.wireOp",EDGE,"E30.1.2.2"),sQuery(id+"F2.wireOp",EDGE,"E30.1.2.3")])]});
            var Q10;
            Q10=makeQuery(id+"F3.opExtrude","SWEPT_BODY",BODY,{"disambiguationData":[OSD([sQuery(id+"F2.wireOp",EDGE,"E30.2.3.0"),sQuery(id+"F2.wireOp",EDGE,"E30.2.3.1"),sQuery(id+"F2.wireOp",EDGE,"E30.2.3.2"),sQuery(id+"F2.wireOp",EDGE,"E30.2.3.3")])]});
            var Q11;
            Q11=makeQuery(id+"F3.opExtrude","SWEPT_BODY",BODY,{"disambiguationData":[OSD([sQuery(id+"F2.wireOp",EDGE,"E30.3.0.0"),sQuery(id+"F2.wireOp",EDGE,"E30.3.0.1"),sQuery(id+"F2.wireOp",EDGE,"E30.3.0.2"),sQuery(id+"F2.wireOp",EDGE,"E30.3.0.3")])]});
            var Q12;
            Q12=makeQuery(id+"F3.opExtrude","SWEPT_BODY",BODY,{"disambiguationData":[OSD([sQuery(id+"F2.wireOp",EDGE,"E30.2.4.0"),sQuery(id+"F2.wireOp",EDGE,"E30.2.4.1"),sQuery(id+"F2.wireOp",EDGE,"E30.2.4.2"),sQuery(id+"F2.wireOp",EDGE,"E30.2.4.3")])]});
            var Q13;
            Q13=makeQuery(id+"F3.opExtrude","SWEPT_BODY",BODY,{"disambiguationData":[OSD([sQuery(id+"F2.wireOp",EDGE,"E30.3.1.0"),sQuery(id+"F2.wireOp",EDGE,"E30.3.1.1"),sQuery(id+"F2.wireOp",EDGE,"E30.3.1.2"),sQuery(id+"F2.wireOp",EDGE,"E30.3.1.3")])]});
            var Q14;
            Q14=makeQuery(id+"F3.opExtrude","SWEPT_BODY",BODY,{"disambiguationData":[OSD([sQuery(id+"F2.wireOp",EDGE,"E30.2.1.0"),sQuery(id+"F2.wireOp",EDGE,"E30.2.1.1"),sQuery(id+"F2.wireOp",EDGE,"E30.2.1.2"),sQuery(id+"F2.wireOp",EDGE,"E30.2.1.3")])]});
            var Q15;
            Q15=makeQuery(id+"F3.opExtrude","SWEPT_BODY",BODY,{"disambiguationData":[OSD([sQuery(id+"F2.wireOp",EDGE,"E30.2.2.0"),sQuery(id+"F2.wireOp",EDGE,"E30.2.2.1"),sQuery(id+"F2.wireOp",EDGE,"E30.2.2.2"),sQuery(id+"F2.wireOp",EDGE,"E30.2.2.3")])]});
            var Q16;
            Q16=makeQuery(id+"F3.opExtrude","SWEPT_BODY",BODY,{"disambiguationData":[OSD([sQuery(id+"F2.wireOp",EDGE,"E30.2.5.0"),sQuery(id+"F2.wireOp",EDGE,"E30.2.5.1"),sQuery(id+"F2.wireOp",EDGE,"E30.2.5.2"),sQuery(id+"F2.wireOp",EDGE,"E30.2.5.3")])]});
            var Q17;
            Q17=makeQuery(id+"F3.opExtrude","SWEPT_BODY",BODY,{"disambiguationData":[OSD([sQuery(id+"F2.wireOp",EDGE,"E30.0.5.0"),sQuery(id+"F2.wireOp",EDGE,"E30.0.5.1"),sQuery(id+"F2.wireOp",EDGE,"E30.0.5.2"),sQuery(id+"F2.wireOp",EDGE,"E30.0.5.3")])]});
            var Q18;
            Q18=makeQuery(id+"F3.opExtrude","SWEPT_BODY",BODY,{"disambiguationData":[OSD([sQuery(id+"F2.wireOp",EDGE,"E30.3.3.0"),sQuery(id+"F2.wireOp",EDGE,"E30.3.3.1"),sQuery(id+"F2.wireOp",EDGE,"E30.3.3.2"),sQuery(id+"F2.wireOp",EDGE,"E30.3.3.3")])]});
            var Q19;
            Q19=makeQuery(id+"F3.opExtrude","SWEPT_BODY",BODY,{"disambiguationData":[OSD([sQuery(id+"F2.wireOp",EDGE,"E30.3.2.0"),sQuery(id+"F2.wireOp",EDGE,"E30.3.2.1"),sQuery(id+"F2.wireOp",EDGE,"E30.3.2.2"),sQuery(id+"F2.wireOp",EDGE,"E30.3.2.3")])]});
            var Q20;
            Q20=makeQuery(id+"F3.opExtrude","SWEPT_BODY",BODY,{"disambiguationData":[OSD([sQuery(id+"F2.wireOp",EDGE,"E30.3.4.0"),sQuery(id+"F2.wireOp",EDGE,"E30.3.4.1"),sQuery(id+"F2.wireOp",EDGE,"E30.3.4.2"),sQuery(id+"F2.wireOp",EDGE,"E30.3.4.3")])]});
            var Q21;
            Q21=makeQuery(id+"F3.opExtrude","SWEPT_BODY",BODY,{"disambiguationData":[OSD([sQuery(id+"F2.wireOp",EDGE,"E30.0.3.0"),sQuery(id+"F2.wireOp",EDGE,"E30.0.3.1"),sQuery(id+"F2.wireOp",EDGE,"E30.0.3.2"),sQuery(id+"F2.wireOp",EDGE,"E30.0.3.3")])]});
            var Q22;
            Q22=makeQuery(id+"F3.opExtrude","SWEPT_BODY",BODY,{"disambiguationData":[OSD([sQuery(id+"F2.wireOp",EDGE,"E30.0.2.0"),sQuery(id+"F2.wireOp",EDGE,"E30.0.2.1"),sQuery(id+"F2.wireOp",EDGE,"E30.0.2.2"),sQuery(id+"F2.wireOp",EDGE,"E30.0.2.3")])]});
            var Q23;
            Q23=makeQuery(id+"F3.opExtrude","SWEPT_BODY",BODY,{"disambiguationData":[OSD([sQuery(id+"F2.wireOp",EDGE,"E30.3.5.0"),sQuery(id+"F2.wireOp",EDGE,"E30.3.5.1"),sQuery(id+"F2.wireOp",EDGE,"E30.3.5.2"),sQuery(id+"F2.wireOp",EDGE,"E30.3.5.3")])]});
            var Q24;
            Q24=makeQuery(id+"F3.opExtrude","SWEPT_BODY",BODY,{"disambiguationData":[OSD([sQuery(id+"F2.wireOp",EDGE,"E30.4.0.0"),sQuery(id+"F2.wireOp",EDGE,"E30.4.0.1"),sQuery(id+"F2.wireOp",EDGE,"E30.4.0.2"),sQuery(id+"F2.wireOp",EDGE,"E30.4.0.3")])]});
            var Q25;
            Q25=makeQuery(id+"F3.opExtrude","SWEPT_BODY",BODY,{"disambiguationData":[OSD([sQuery(id+"F2.wireOp",EDGE,"E30.4.3.0"),sQuery(id+"F2.wireOp",EDGE,"E30.4.3.1"),sQuery(id+"F2.wireOp",EDGE,"E30.4.3.2"),sQuery(id+"F2.wireOp",EDGE,"E30.4.3.3")])]});
            var Q26;
            Q26=makeQuery(id+"F3.opExtrude","SWEPT_BODY",BODY,{"disambiguationData":[OSD([sQuery(id+"F2.wireOp",EDGE,"E30.4.1.0"),sQuery(id+"F2.wireOp",EDGE,"E30.4.1.1"),sQuery(id+"F2.wireOp",EDGE,"E30.4.1.2"),sQuery(id+"F2.wireOp",EDGE,"E30.4.1.3")])]});
            var Q27;
            Q27=makeQuery(id+"F3.opExtrude","SWEPT_BODY",BODY,{"disambiguationData":[OSD([sQuery(id+"F2.wireOp",EDGE,"E30.4.2.0"),sQuery(id+"F2.wireOp",EDGE,"E30.4.2.1"),sQuery(id+"F2.wireOp",EDGE,"E30.4.2.2"),sQuery(id+"F2.wireOp",EDGE,"E30.4.2.3")])]});
            var Q28;
            Q28=makeQuery(id+"F3.opExtrude","SWEPT_BODY",BODY,{"disambiguationData":[OSD([sQuery(id+"F2.wireOp",EDGE,"E30.5.2.0"),sQuery(id+"F2.wireOp",EDGE,"E30.5.2.1"),sQuery(id+"F2.wireOp",EDGE,"E30.5.2.2"),sQuery(id+"F2.wireOp",EDGE,"E30.5.2.3")])]});
            var Q29;
            Q29=makeQuery(id+"F3.opExtrude","SWEPT_BODY",BODY,{"disambiguationData":[OSD([sQuery(id+"F2.wireOp",EDGE,"E30.5.3.0"),sQuery(id+"F2.wireOp",EDGE,"E30.5.3.1"),sQuery(id+"F2.wireOp",EDGE,"E30.5.3.2"),sQuery(id+"F2.wireOp",EDGE,"E30.5.3.3")])]});
            var Q30;
            Q30=makeQuery(id+"F3.opExtrude","SWEPT_BODY",BODY,{"disambiguationData":[OSD([sQuery(id+"F2.wireOp",EDGE,"E30.5.4.0"),sQuery(id+"F2.wireOp",EDGE,"E30.5.4.1"),sQuery(id+"F2.wireOp",EDGE,"E30.5.4.2"),sQuery(id+"F2.wireOp",EDGE,"E30.5.4.3")])]});
            var Q31;
            Q31=makeQuery(id+"F3.opExtrude","SWEPT_BODY",BODY,{"disambiguationData":[OSD([sQuery(id+"F2.wireOp",EDGE,"E30.0.1.0"),sQuery(id+"F2.wireOp",EDGE,"E30.0.1.1"),sQuery(id+"F2.wireOp",EDGE,"E30.0.1.2"),sQuery(id+"F2.wireOp",EDGE,"E30.0.1.3")])]});
            var Q32;
            Q32=makeQuery(id+"F3.opExtrude","SWEPT_BODY",BODY,{"disambiguationData":[OSD([sQuery(id+"F2.wireOp",EDGE,"E29.bottom"),sQuery(id+"F2.wireOp",EDGE,"E29.top"),sQuery(id+"F2.wireOp",EDGE,"E29.left"),sQuery(id+"F2.wireOp",EDGE,"E29.right")])]});
            var Q33;
            Q33=makeQuery(id+"F5.opPattern","COPY",BODY,{"derivedFrom":makeQuery(id+"F3.opExtrude","SWEPT_BODY",BODY,{"disambiguationData":[OSD([sQuery(id+"F2.wireOp",EDGE,"E30.0.2.0"),sQuery(id+"F2.wireOp",EDGE,"E30.0.2.1"),sQuery(id+"F2.wireOp",EDGE,"E30.0.2.2"),sQuery(id+"F2.wireOp",EDGE,"E30.0.2.3")])]}),"instanceName":"1"});
            var Q34;
            Q34=makeQuery(id+"F5.opPattern","COPY",BODY,{"derivedFrom":makeQuery(id+"F3.opExtrude","SWEPT_BODY",BODY,{"disambiguationData":[OSD([sQuery(id+"F2.wireOp",EDGE,"E30.0.3.0"),sQuery(id+"F2.wireOp",EDGE,"E30.0.3.1"),sQuery(id+"F2.wireOp",EDGE,"E30.0.3.2"),sQuery(id+"F2.wireOp",EDGE,"E30.0.3.3")])]}),"instanceName":"1"});
            var Q35;
            Q35=makeQuery(id+"F5.opPattern","COPY",BODY,{"derivedFrom":makeQuery(id+"F3.opExtrude","SWEPT_BODY",BODY,{"disambiguationData":[OSD([sQuery(id+"F2.wireOp",EDGE,"E30.0.1.0"),sQuery(id+"F2.wireOp",EDGE,"E30.0.1.1"),sQuery(id+"F2.wireOp",EDGE,"E30.0.1.2"),sQuery(id+"F2.wireOp",EDGE,"E30.0.1.3")])]}),"instanceName":"1"});
            var Q36;
            Q36=makeQuery(id+"F5.opPattern","COPY",BODY,{"derivedFrom":makeQuery(id+"F3.opExtrude","SWEPT_BODY",BODY,{"disambiguationData":[OSD([sQuery(id+"F2.wireOp",EDGE,"E29.bottom"),sQuery(id+"F2.wireOp",EDGE,"E29.top"),sQuery(id+"F2.wireOp",EDGE,"E29.left"),sQuery(id+"F2.wireOp",EDGE,"E29.right")])]}),"instanceName":"1"});
            var Q37;
            Q37=makeQuery(id+"F5.opPattern","COPY",BODY,{"derivedFrom":makeQuery(id+"F3.opExtrude","SWEPT_BODY",BODY,{"disambiguationData":[OSD([sQuery(id+"F2.wireOp",EDGE,"E30.0.4.0"),sQuery(id+"F2.wireOp",EDGE,"E30.0.4.1"),sQuery(id+"F2.wireOp",EDGE,"E30.0.4.2"),sQuery(id+"F2.wireOp",EDGE,"E30.0.4.3")])]}),"instanceName":"1"});
            var Q38;
            Q38=makeQuery(id+"F5.opPattern","COPY",BODY,{"derivedFrom":makeQuery(id+"F3.opExtrude","SWEPT_BODY",BODY,{"disambiguationData":[OSD([sQuery(id+"F2.wireOp",EDGE,"E30.0.5.0"),sQuery(id+"F2.wireOp",EDGE,"E30.0.5.1"),sQuery(id+"F2.wireOp",EDGE,"E30.0.5.2"),sQuery(id+"F2.wireOp",EDGE,"E30.0.5.3")])]}),"instanceName":"1"});
            var Q39;
            Q39=makeQuery(id+"F5.opPattern","COPY",BODY,{"derivedFrom":makeQuery(id+"F3.opExtrude","SWEPT_BODY",BODY,{"disambiguationData":[OSD([sQuery(id+"F2.wireOp",EDGE,"E30.1.0.0"),sQuery(id+"F2.wireOp",EDGE,"E30.1.0.1"),sQuery(id+"F2.wireOp",EDGE,"E30.1.0.2"),sQuery(id+"F2.wireOp",EDGE,"E30.1.0.3")])]}),"instanceName":"1"});
            var Q40;
            Q40=makeQuery(id+"F5.opPattern","COPY",BODY,{"derivedFrom":makeQuery(id+"F3.opExtrude","SWEPT_BODY",BODY,{"disambiguationData":[OSD([sQuery(id+"F2.wireOp",EDGE,"E30.1.1.0"),sQuery(id+"F2.wireOp",EDGE,"E30.1.1.1"),sQuery(id+"F2.wireOp",EDGE,"E30.1.1.2"),sQuery(id+"F2.wireOp",EDGE,"E30.1.1.3")])]}),"instanceName":"1"});
            var Q41;
            Q41=makeQuery(id+"F5.opPattern","COPY",BODY,{"derivedFrom":makeQuery(id+"F3.opExtrude","SWEPT_BODY",BODY,{"disambiguationData":[OSD([sQuery(id+"F2.wireOp",EDGE,"E30.1.2.0"),sQuery(id+"F2.wireOp",EDGE,"E30.1.2.1"),sQuery(id+"F2.wireOp",EDGE,"E30.1.2.2"),sQuery(id+"F2.wireOp",EDGE,"E30.1.2.3")])]}),"instanceName":"1"});
            var Q42;
            Q42=makeQuery(id+"F5.opPattern","COPY",BODY,{"derivedFrom":makeQuery(id+"F3.opExtrude","SWEPT_BODY",BODY,{"disambiguationData":[OSD([sQuery(id+"F2.wireOp",EDGE,"E30.1.3.0"),sQuery(id+"F2.wireOp",EDGE,"E30.1.3.1"),sQuery(id+"F2.wireOp",EDGE,"E30.1.3.2"),sQuery(id+"F2.wireOp",EDGE,"E30.1.3.3")])]}),"instanceName":"1"});
            var Q43;
            Q43=makeQuery(id+"F3.opExtrude","SWEPT_BODY",BODY,{"disambiguationData":[OSD([sQuery(id+"F2.wireOp",EDGE,"E30.2.0.0"),sQuery(id+"F2.wireOp",EDGE,"E30.2.0.1"),sQuery(id+"F2.wireOp",EDGE,"E30.2.0.2"),sQuery(id+"F2.wireOp",EDGE,"E30.2.0.3")])]});
            var Q44;
            Q44=makeQuery(id+"F3.opExtrude","SWEPT_BODY",BODY,{"disambiguationData":[OSD([sQuery(id+"F2.wireOp",EDGE,"E30.0.4.0"),sQuery(id+"F2.wireOp",EDGE,"E30.0.4.1"),sQuery(id+"F2.wireOp",EDGE,"E30.0.4.2"),sQuery(id+"F2.wireOp",EDGE,"E30.0.4.3")])]});
            var Q45;
            Q45=makeQuery(id+"F5.opPattern","COPY",BODY,{"derivedFrom":makeQuery(id+"F3.opExtrude","SWEPT_BODY",BODY,{"disambiguationData":[OSD([sQuery(id+"F2.wireOp",EDGE,"E30.1.5.0"),sQuery(id+"F2.wireOp",EDGE,"E30.1.5.1"),sQuery(id+"F2.wireOp",EDGE,"E30.1.5.2"),sQuery(id+"F2.wireOp",EDGE,"E30.1.5.3")])]}),"instanceName":"1"});
            var Q46;
            Q46=makeQuery(id+"F5.opPattern","COPY",BODY,{"derivedFrom":makeQuery(id+"F3.opExtrude","SWEPT_BODY",BODY,{"disambiguationData":[OSD([sQuery(id+"F2.wireOp",EDGE,"E30.1.4.0"),sQuery(id+"F2.wireOp",EDGE,"E30.1.4.1"),sQuery(id+"F2.wireOp",EDGE,"E30.1.4.2"),sQuery(id+"F2.wireOp",EDGE,"E30.1.4.3")])]}),"instanceName":"1"});
            var Q47;
            Q47=makeQuery(id+"F5.opPattern","COPY",BODY,{"derivedFrom":makeQuery(id+"F3.opExtrude","SWEPT_BODY",BODY,{"disambiguationData":[OSD([sQuery(id+"F2.wireOp",EDGE,"E30.2.0.0"),sQuery(id+"F2.wireOp",EDGE,"E30.2.0.1"),sQuery(id+"F2.wireOp",EDGE,"E30.2.0.2"),sQuery(id+"F2.wireOp",EDGE,"E30.2.0.3")])]}),"instanceName":"1"});
            var Q48;
            Q48=makeQuery(id+"F5.opPattern","COPY",BODY,{"derivedFrom":makeQuery(id+"F3.opExtrude","SWEPT_BODY",BODY,{"disambiguationData":[OSD([sQuery(id+"F2.wireOp",EDGE,"E30.2.1.0"),sQuery(id+"F2.wireOp",EDGE,"E30.2.1.1"),sQuery(id+"F2.wireOp",EDGE,"E30.2.1.2"),sQuery(id+"F2.wireOp",EDGE,"E30.2.1.3")])]}),"instanceName":"1"});
            var Q49;
            Q49=makeQuery(id+"F5.opPattern","COPY",BODY,{"derivedFrom":makeQuery(id+"F3.opExtrude","SWEPT_BODY",BODY,{"disambiguationData":[OSD([sQuery(id+"F2.wireOp",EDGE,"E30.2.2.0"),sQuery(id+"F2.wireOp",EDGE,"E30.2.2.1"),sQuery(id+"F2.wireOp",EDGE,"E30.2.2.2"),sQuery(id+"F2.wireOp",EDGE,"E30.2.2.3")])]}),"instanceName":"1"});
            var Q50;
            Q50=makeQuery(id+"F5.opPattern","COPY",BODY,{"derivedFrom":makeQuery(id+"F3.opExtrude","SWEPT_BODY",BODY,{"disambiguationData":[OSD([sQuery(id+"F2.wireOp",EDGE,"E30.2.3.0"),sQuery(id+"F2.wireOp",EDGE,"E30.2.3.1"),sQuery(id+"F2.wireOp",EDGE,"E30.2.3.2"),sQuery(id+"F2.wireOp",EDGE,"E30.2.3.3")])]}),"instanceName":"1"});
            var Q51;
            Q51=makeQuery(id+"F5.opPattern","COPY",BODY,{"derivedFrom":makeQuery(id+"F3.opExtrude","SWEPT_BODY",BODY,{"disambiguationData":[OSD([sQuery(id+"F2.wireOp",EDGE,"E30.2.5.0"),sQuery(id+"F2.wireOp",EDGE,"E30.2.5.1"),sQuery(id+"F2.wireOp",EDGE,"E30.2.5.2"),sQuery(id+"F2.wireOp",EDGE,"E30.2.5.3")])]}),"instanceName":"1"});
            var Q52;
            Q52=makeQuery(id+"F5.opPattern","COPY",BODY,{"derivedFrom":makeQuery(id+"F3.opExtrude","SWEPT_BODY",BODY,{"disambiguationData":[OSD([sQuery(id+"F2.wireOp",EDGE,"E30.3.0.0"),sQuery(id+"F2.wireOp",EDGE,"E30.3.0.1"),sQuery(id+"F2.wireOp",EDGE,"E30.3.0.2"),sQuery(id+"F2.wireOp",EDGE,"E30.3.0.3")])]}),"instanceName":"1"});
            var Q53;
            Q53=makeQuery(id+"F5.opPattern","COPY",BODY,{"derivedFrom":makeQuery(id+"F3.opExtrude","SWEPT_BODY",BODY,{"disambiguationData":[OSD([sQuery(id+"F2.wireOp",EDGE,"E30.3.1.0"),sQuery(id+"F2.wireOp",EDGE,"E30.3.1.1"),sQuery(id+"F2.wireOp",EDGE,"E30.3.1.2"),sQuery(id+"F2.wireOp",EDGE,"E30.3.1.3")])]}),"instanceName":"1"});
            var Q54;
            Q54=makeQuery(id+"F5.opPattern","COPY",BODY,{"derivedFrom":makeQuery(id+"F3.opExtrude","SWEPT_BODY",BODY,{"disambiguationData":[OSD([sQuery(id+"F2.wireOp",EDGE,"E30.3.2.0"),sQuery(id+"F2.wireOp",EDGE,"E30.3.2.1"),sQuery(id+"F2.wireOp",EDGE,"E30.3.2.2"),sQuery(id+"F2.wireOp",EDGE,"E30.3.2.3")])]}),"instanceName":"1"});
            var Q55;
            Q55=makeQuery(id+"F5.opPattern","COPY",BODY,{"derivedFrom":makeQuery(id+"F3.opExtrude","SWEPT_BODY",BODY,{"disambiguationData":[OSD([sQuery(id+"F2.wireOp",EDGE,"E30.4.4.0"),sQuery(id+"F2.wireOp",EDGE,"E30.4.4.1"),sQuery(id+"F2.wireOp",EDGE,"E30.4.4.2"),sQuery(id+"F2.wireOp",EDGE,"E30.4.4.3")])]}),"instanceName":"1"});
            var Q56;
            Q56=makeQuery(id+"F5.opPattern","COPY",BODY,{"derivedFrom":makeQuery(id+"F3.opExtrude","SWEPT_BODY",BODY,{"disambiguationData":[OSD([sQuery(id+"F2.wireOp",EDGE,"E30.3.3.0"),sQuery(id+"F2.wireOp",EDGE,"E30.3.3.1"),sQuery(id+"F2.wireOp",EDGE,"E30.3.3.2"),sQuery(id+"F2.wireOp",EDGE,"E30.3.3.3")])]}),"instanceName":"1"});
            var Q57;
            Q57=makeQuery(id+"F5.opPattern","COPY",BODY,{"derivedFrom":makeQuery(id+"F3.opExtrude","SWEPT_BODY",BODY,{"disambiguationData":[OSD([sQuery(id+"F2.wireOp",EDGE,"E30.3.4.0"),sQuery(id+"F2.wireOp",EDGE,"E30.3.4.1"),sQuery(id+"F2.wireOp",EDGE,"E30.3.4.2"),sQuery(id+"F2.wireOp",EDGE,"E30.3.4.3")])]}),"instanceName":"1"});
            var Q58;
            Q58=makeQuery(id+"F5.opPattern","COPY",BODY,{"derivedFrom":makeQuery(id+"F3.opExtrude","SWEPT_BODY",BODY,{"disambiguationData":[OSD([sQuery(id+"F2.wireOp",EDGE,"E30.2.4.0"),sQuery(id+"F2.wireOp",EDGE,"E30.2.4.1"),sQuery(id+"F2.wireOp",EDGE,"E30.2.4.2"),sQuery(id+"F2.wireOp",EDGE,"E30.2.4.3")])]}),"instanceName":"1"});
            var Q59;
            Q59=makeQuery(id+"F5.opPattern","COPY",BODY,{"derivedFrom":makeQuery(id+"F3.opExtrude","SWEPT_BODY",BODY,{"disambiguationData":[OSD([sQuery(id+"F2.wireOp",EDGE,"E30.5.4.0"),sQuery(id+"F2.wireOp",EDGE,"E30.5.4.1"),sQuery(id+"F2.wireOp",EDGE,"E30.5.4.2"),sQuery(id+"F2.wireOp",EDGE,"E30.5.4.3")])]}),"instanceName":"1"});
            var Q60;
            Q60=makeQuery(id+"F5.opPattern","COPY",BODY,{"derivedFrom":makeQuery(id+"F3.opExtrude","SWEPT_BODY",BODY,{"disambiguationData":[OSD([sQuery(id+"F2.wireOp",EDGE,"E30.5.3.0"),sQuery(id+"F2.wireOp",EDGE,"E30.5.3.1"),sQuery(id+"F2.wireOp",EDGE,"E30.5.3.2"),sQuery(id+"F2.wireOp",EDGE,"E30.5.3.3")])]}),"instanceName":"1"});
            var Q61;
            Q61=makeQuery(id+"F5.opPattern","COPY",BODY,{"derivedFrom":makeQuery(id+"F3.opExtrude","SWEPT_BODY",BODY,{"disambiguationData":[OSD([sQuery(id+"F2.wireOp",EDGE,"E30.5.2.0"),sQuery(id+"F2.wireOp",EDGE,"E30.5.2.1"),sQuery(id+"F2.wireOp",EDGE,"E30.5.2.2"),sQuery(id+"F2.wireOp",EDGE,"E30.5.2.3")])]}),"instanceName":"1"});
            var Q62;
            Q62=makeQuery(id+"F5.opPattern","COPY",BODY,{"derivedFrom":makeQuery(id+"F3.opExtrude","SWEPT_BODY",BODY,{"disambiguationData":[OSD([sQuery(id+"F2.wireOp",EDGE,"E30.5.1.0"),sQuery(id+"F2.wireOp",EDGE,"E30.5.1.1"),sQuery(id+"F2.wireOp",EDGE,"E30.5.1.2"),sQuery(id+"F2.wireOp",EDGE,"E30.5.1.3")])]}),"instanceName":"1"});
            var Q63;
            Q63=makeQuery(id+"F5.opPattern","COPY",BODY,{"derivedFrom":makeQuery(id+"F3.opExtrude","SWEPT_BODY",BODY,{"disambiguationData":[OSD([sQuery(id+"F2.wireOp",EDGE,"E30.5.0.0"),sQuery(id+"F2.wireOp",EDGE,"E30.5.0.1"),sQuery(id+"F2.wireOp",EDGE,"E30.5.0.2"),sQuery(id+"F2.wireOp",EDGE,"E30.5.0.3")])]}),"instanceName":"1"});
            var Q64;
            Q64=makeQuery(id+"F5.opPattern","COPY",BODY,{"derivedFrom":makeQuery(id+"F3.opExtrude","SWEPT_BODY",BODY,{"disambiguationData":[OSD([sQuery(id+"F2.wireOp",EDGE,"E30.4.5.0"),sQuery(id+"F2.wireOp",EDGE,"E30.4.5.1"),sQuery(id+"F2.wireOp",EDGE,"E30.4.5.2"),sQuery(id+"F2.wireOp",EDGE,"E30.4.5.3")])]}),"instanceName":"1"});
            var Q65;
            Q65=makeQuery(id+"F5.opPattern","COPY",BODY,{"derivedFrom":makeQuery(id+"F3.opExtrude","SWEPT_BODY",BODY,{"disambiguationData":[OSD([sQuery(id+"F2.wireOp",EDGE,"E30.3.5.0"),sQuery(id+"F2.wireOp",EDGE,"E30.3.5.1"),sQuery(id+"F2.wireOp",EDGE,"E30.3.5.2"),sQuery(id+"F2.wireOp",EDGE,"E30.3.5.3")])]}),"instanceName":"1"});
            var Q66;
            Q66=makeQuery(id+"F5.opPattern","COPY",BODY,{"derivedFrom":makeQuery(id+"F3.opExtrude","SWEPT_BODY",BODY,{"disambiguationData":[OSD([sQuery(id+"F2.wireOp",EDGE,"E30.4.0.0"),sQuery(id+"F2.wireOp",EDGE,"E30.4.0.1"),sQuery(id+"F2.wireOp",EDGE,"E30.4.0.2"),sQuery(id+"F2.wireOp",EDGE,"E30.4.0.3")])]}),"instanceName":"1"});
            var Q67;
            Q67=makeQuery(id+"F5.opPattern","COPY",BODY,{"derivedFrom":makeQuery(id+"F3.opExtrude","SWEPT_BODY",BODY,{"disambiguationData":[OSD([sQuery(id+"F2.wireOp",EDGE,"E30.4.1.0"),sQuery(id+"F2.wireOp",EDGE,"E30.4.1.1"),sQuery(id+"F2.wireOp",EDGE,"E30.4.1.2"),sQuery(id+"F2.wireOp",EDGE,"E30.4.1.3")])]}),"instanceName":"1"});
            var Q68;
            Q68=makeQuery(id+"F5.opPattern","COPY",BODY,{"derivedFrom":makeQuery(id+"F3.opExtrude","SWEPT_BODY",BODY,{"disambiguationData":[OSD([sQuery(id+"F2.wireOp",EDGE,"E30.4.2.0"),sQuery(id+"F2.wireOp",EDGE,"E30.4.2.1"),sQuery(id+"F2.wireOp",EDGE,"E30.4.2.2"),sQuery(id+"F2.wireOp",EDGE,"E30.4.2.3")])]}),"instanceName":"1"});
            var Q69;
            Q69=makeQuery(id+"F5.opPattern","COPY",BODY,{"derivedFrom":makeQuery(id+"F3.opExtrude","SWEPT_BODY",BODY,{"disambiguationData":[OSD([sQuery(id+"F2.wireOp",EDGE,"E30.4.3.0"),sQuery(id+"F2.wireOp",EDGE,"E30.4.3.1"),sQuery(id+"F2.wireOp",EDGE,"E30.4.3.2"),sQuery(id+"F2.wireOp",EDGE,"E30.4.3.3")])]}),"instanceName":"1"});
            var Q70;
            Q70=qCreatedBy(makeId("Front.planeOp"),FACE);
            mirror(context, id + "F6", {"entities" : qUnion([Q0, Q1, Q2, Q3, Q4, Q5, Q6, Q7, Q8, Q9, Q10, Q11, Q12, Q13, Q14, Q15, Q16, Q17, Q18, Q19, Q20, Q21, Q22, Q23, Q24, Q25, Q26, Q27, Q28, Q29, Q30, Q31, Q32, Q33, Q34, Q35, Q36, Q37, Q38, Q39, Q40, Q41, Q42, Q43, Q44, Q45, Q46, Q47, Q48, Q49, Q50, Q51, Q52, Q53, Q54, Q55, Q56, Q57, Q58, Q59, Q60, Q61, Q62, Q63, Q64, Q65, Q66, Q67, Q68, Q69]), "mirrorPlane" : qUnion([Q70])});
        }
        {
            var Q0;
            Q0=makeQuery(id+"F0.imprint","IMPRINT",FACE,{"disambiguationData":[TD([[makeQuery(id+"F0.imprint","IMPRINT",EDGE,{"derivedFrom":sQuery(id+"F0.wireOp",EDGE,"E0")}),-1.0]])]});
            var Q1;
            {var subQ2=sQuery(id+"F0.wireOp",EDGE,"E2.bottom");Q1=makeQuery(id+"F0.imprint","IMPRINT",FACE,{"disambiguationData":[TD([[makeQuery(id+"F0.imprint","IMPRINT",EDGE,{"derivedFrom":subQ2}),1.0]])]});}
            var Q2;
            Q2=makeQuery(id+"F0.imprint","IMPRINT",FACE,{"disambiguationData":[TD([[makeQuery(id+"F0.imprint","IMPRINT",EDGE,{"derivedFrom":sQuery(id+"F0.wireOp",EDGE,"E14.MirrorCS")}),1.0]])]});
            var Q3;
            {var subQ1=sQuery(id+"F0.wireOp",EDGE,"E18.MirrorCS");Q3=makeQuery(id+"F0.imprint","IMPRINT",FACE,{"disambiguationData":[TD([[makeQuery(id+"F0.imprint","IMPRINT",EDGE,{"derivedFrom":subQ1}),1.0]])]});}
            extrude(context, id + "F7", {"entities" : qUnion([Q0, Q1, Q2, Q3]), "operationType" : NewBodyOperationType.ADD, "depth" : 0.2 * mm});
        }
    });
